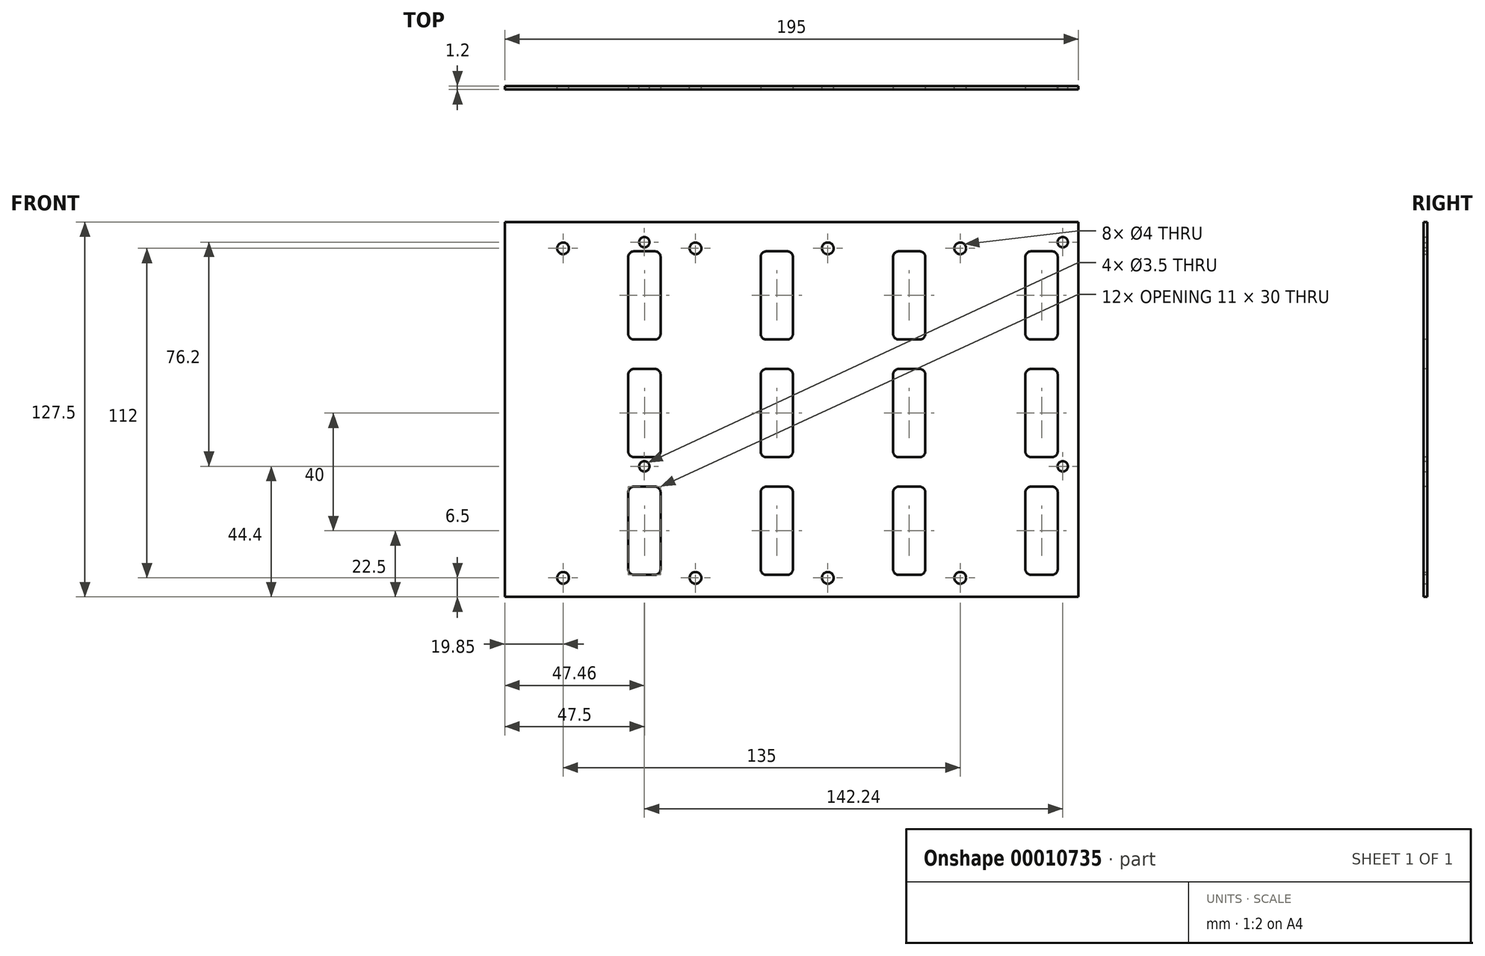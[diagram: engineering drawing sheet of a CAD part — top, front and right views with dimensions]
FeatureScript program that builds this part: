
annotation { "Feature Type Name" : "Feature", "Feature Type Description" : "" }
export const myFeature = defineFeature(function(context is Context, id is Id, definition is map)
    precondition{}
    {
        {
            var Q0;
            Q0=qCreatedBy(makeId("Front.planeOp"),FACE);
            var sketch = newSketch(context, id + "F0", { "sketchPlane" : qUnion([Q0])});
            skLineSegment(sketch, "E0.bottom", {"start": v(0, 0) * mm, "end": v(200, 0) * mm});
            skLineSegment(sketch, "E0.top", {"start": v(0, 130) * mm, "end": v(200, 130) * mm});
            skLineSegment(sketch, "E0.left", {"start": v(0, 0) * mm, "end": v(0, 130) * mm});
            skLineSegment(sketch, "E0.right", {"start": v(200, 0) * mm, "end": v(200, 130) * mm});
            skCircle(sketch, "E1", {"center": v(24.85, 9) * mm, "radius": 2 * mm});
            skCircle(sketch, "E2.0.1.0", {"center": v(24.85, 121) * mm, "radius": 2 * mm});
            skCircle(sketch, "E2.1.0.0", {"center": v(69.85, 9) * mm, "radius": 2 * mm});
            skCircle(sketch, "E2.1.1.0", {"center": v(69.85, 121) * mm, "radius": 2 * mm});
            skCircle(sketch, "E2.2.0.0", {"center": v(114.85, 9) * mm, "radius": 2 * mm});
            skCircle(sketch, "E2.2.1.0", {"center": v(114.85, 121) * mm, "radius": 2 * mm});
            skLineSegment(sketch, "E2.direction1", {"start": v(24.85, 9) * mm, "end": v(69.85, 9) * mm, "construction": true});
            skLineSegment(sketch, "E2.direction2", {"start": v(24.85, 9) * mm, "end": v(24.85, 121) * mm, "construction": true});
            skCircle(sketch, "E3.0.3.0", {"center": v(159.85, 9) * mm, "radius": 2 * mm});
            skCircle(sketch, "E3.0.3.1", {"center": v(159.85, 121) * mm, "radius": 2 * mm});
            skLineSegment(sketch, "E4", {"start": v(200, 65) * mm, "end": v(0, 65) * mm, "construction": true});
            skPoint(sketch, "E4.endSnap0", {"position": v(0, 65) * mm});
            skPoint(sketch, "E4.endSnap1", {"position": v(24.85, 65) * mm});
            skSolve(sketch);
        }
        {
            var Q0;
            Q0=makeQuery(id+"F0.imprint","IMPRINT",FACE,{"disambiguationData":[TD([[makeQuery(id+"F0.imprint","IMPRINT",EDGE,{"derivedFrom":sQuery(id+"F0.wireOp",EDGE,"E0.bottom")}),1.0]])]});
            extrude(context, id + "F1", {"entities" : qUnion([Q0]), "depth" : 1.2 * mm});
        }
        {
            var Q0;
            Q0=makeQuery(id+"F1.opExtrude","CAP_FACE",FACE,{"disambiguationData":[OSD([sQuery(id+"F0.wireOp",EDGE,"E0.bottom"),sQuery(id+"F0.wireOp",EDGE,"E0.top"),sQuery(id+"F0.wireOp",EDGE,"E0.left"),sQuery(id+"F0.wireOp",EDGE,"E0.right"),sQuery(id+"F0.wireOp",EDGE,"E1"),sQuery(id+"F0.wireOp",EDGE,"E2.0.1.0"),sQuery(id+"F0.wireOp",EDGE,"E2.1.0.0"),sQuery(id+"F0.wireOp",EDGE,"E2.1.1.0"),sQuery(id+"F0.wireOp",EDGE,"E2.2.0.0"),sQuery(id+"F0.wireOp",EDGE,"E2.2.1.0"),sQuery(id+"F0.wireOp",EDGE,"E3.0.3.0"),sQuery(id+"F0.wireOp",EDGE,"E3.0.3.1")])],"isStart":false});
            var sketch = newSketch(context, id + "F2", { "sketchPlane" : qUnion([Q0])});
            skLineSegment(sketch, "E5.bottom", {"start": v(49, 10) * mm, "end": v(56, 10) * mm});
            skLineSegment(sketch, "E5.top", {"start": v(49, 40) * mm, "end": v(56, 40) * mm});
            skLineSegment(sketch, "E5.left", {"start": v(47, 12) * mm, "end": v(47, 38) * mm});
            skLineSegment(sketch, "E5.right", {"start": v(58, 12) * mm, "end": v(58, 38) * mm});
            skPoint(sketch, "E6", {"position": v(24.85, 9) * mm});
            skLineSegment(sketch, "E7.bottom", {"start": v(49, 50) * mm, "end": v(56, 50) * mm});
            skLineSegment(sketch, "E7.top", {"start": v(49, 80) * mm, "end": v(56, 80) * mm});
            skLineSegment(sketch, "E7.left", {"start": v(47, 52) * mm, "end": v(47, 78) * mm});
            skLineSegment(sketch, "E7.right", {"start": v(58, 52) * mm, "end": v(58, 78) * mm});
            skLineSegment(sketch, "E8.bottom", {"start": v(49, 90) * mm, "end": v(56, 90) * mm});
            skLineSegment(sketch, "E8.top", {"start": v(49, 120) * mm, "end": v(56, 120) * mm});
            skLineSegment(sketch, "E8.left", {"start": v(47, 92) * mm, "end": v(47, 118) * mm});
            skLineSegment(sketch, "E8.right", {"start": v(58, 92) * mm, "end": v(58, 118) * mm});
            skLineSegment(sketch, "E9", {"start": v(0, 65) * mm, "end": v(200, 65) * mm, "construction": true});
            skPoint(sketch, "E10.visualSharp", {"position": v(47, 40) * mm});
            skArc(sketch, "E10.filletArc", {"start": v(49, 40) * mm, "mid": v(47.59, 39.41) * mm, "end": v(47, 38) * mm});
            skPoint(sketch, "E11.visualSharp", {"position": v(58, 40) * mm});
            skArc(sketch, "E11.filletArc", {"start": v(58, 38) * mm, "mid": v(57.41, 39.41) * mm, "end": v(56, 40) * mm});
            skPoint(sketch, "E12.visualSharp", {"position": v(58, 10) * mm});
            skArc(sketch, "E12.filletArc", {"start": v(56, 10) * mm, "mid": v(57.41, 10.59) * mm, "end": v(58, 12) * mm});
            skPoint(sketch, "E13.visualSharp", {"position": v(47, 10) * mm});
            skArc(sketch, "E13.filletArc", {"start": v(47, 12) * mm, "mid": v(47.59, 10.59) * mm, "end": v(49, 10) * mm});
            skPoint(sketch, "E14.visualSharp", {"position": v(47, 50) * mm});
            skArc(sketch, "E14.filletArc", {"start": v(47, 52) * mm, "mid": v(47.59, 50.59) * mm, "end": v(49, 50) * mm});
            skPoint(sketch, "E15.visualSharp", {"position": v(58, 50) * mm});
            skArc(sketch, "E15.filletArc", {"start": v(56, 50) * mm, "mid": v(57.41, 50.59) * mm, "end": v(58, 52) * mm});
            skPoint(sketch, "E16.visualSharp", {"position": v(47, 80) * mm});
            skArc(sketch, "E16.filletArc", {"start": v(49, 80) * mm, "mid": v(47.59, 79.41) * mm, "end": v(47, 78) * mm});
            skPoint(sketch, "E17.visualSharp", {"position": v(58, 80) * mm});
            skArc(sketch, "E17.filletArc", {"start": v(58, 78) * mm, "mid": v(57.41, 79.41) * mm, "end": v(56, 80) * mm});
            skPoint(sketch, "E18.visualSharp", {"position": v(58, 90) * mm});
            skArc(sketch, "E18.filletArc", {"start": v(56, 90) * mm, "mid": v(57.41, 90.59) * mm, "end": v(58, 92) * mm});
            skPoint(sketch, "E19.visualSharp", {"position": v(47, 90) * mm});
            skArc(sketch, "E19.filletArc", {"start": v(47, 92) * mm, "mid": v(47.59, 90.59) * mm, "end": v(49, 90) * mm});
            skPoint(sketch, "E20.visualSharp", {"position": v(47, 120) * mm});
            skArc(sketch, "E20.filletArc", {"start": v(49, 120) * mm, "mid": v(47.59, 119.41) * mm, "end": v(47, 118) * mm});
            skPoint(sketch, "E21.visualSharp", {"position": v(58, 120) * mm});
            skArc(sketch, "E21.filletArc", {"start": v(58, 118) * mm, "mid": v(57.41, 119.41) * mm, "end": v(56, 120) * mm});
            skPoint(sketch, "E22.1.0.0", {"position": v(103, 120) * mm});
            skPoint(sketch, "E22.1.0.1", {"position": v(103, 90) * mm});
            skPoint(sketch, "E22.1.0.2", {"position": v(92, 80) * mm});
            skPoint(sketch, "E22.1.0.3", {"position": v(92, 10) * mm});
            skPoint(sketch, "E22.1.0.4", {"position": v(103, 80) * mm});
            skPoint(sketch, "E22.1.0.5", {"position": v(103, 40) * mm});
            skPoint(sketch, "E22.1.0.6", {"position": v(92, 40) * mm});
            skPoint(sketch, "E22.1.0.7", {"position": v(92, 90) * mm});
            skLineSegment(sketch, "E22.1.0.8", {"start": v(92, 92) * mm, "end": v(92, 118) * mm});
            skLineSegment(sketch, "E22.1.0.9", {"start": v(103, 92) * mm, "end": v(103, 118) * mm});
            skPoint(sketch, "E22.1.0.10", {"position": v(92, 120) * mm});
            skPoint(sketch, "E22.1.0.11", {"position": v(92, 50) * mm});
            skPoint(sketch, "E22.1.0.12", {"position": v(103, 10) * mm});
            skPoint(sketch, "E22.1.0.13", {"position": v(103, 50) * mm});
            skLineSegment(sketch, "E22.1.0.14", {"start": v(92, 12) * mm, "end": v(92, 38) * mm});
            skLineSegment(sketch, "E22.1.0.15", {"start": v(103, 12) * mm, "end": v(103, 38) * mm});
            skLineSegment(sketch, "E22.1.0.16", {"start": v(92, 52) * mm, "end": v(92, 78) * mm});
            skLineSegment(sketch, "E22.1.0.17", {"start": v(103, 52) * mm, "end": v(103, 78) * mm});
            skArc(sketch, "E22.1.0.18", {"start": v(92, 52) * mm, "mid": v(92.59, 50.59) * mm, "end": v(94, 50) * mm});
            skArc(sketch, "E22.1.0.19", {"start": v(101, 50) * mm, "mid": v(102.41, 50.59) * mm, "end": v(103, 52) * mm});
            skArc(sketch, "E22.1.0.20", {"start": v(92, 92) * mm, "mid": v(92.59, 90.59) * mm, "end": v(94, 90) * mm});
            skArc(sketch, "E22.1.0.21", {"start": v(101, 90) * mm, "mid": v(102.41, 90.59) * mm, "end": v(103, 92) * mm});
            skArc(sketch, "E22.1.0.22", {"start": v(103, 118) * mm, "mid": v(102.41, 119.41) * mm, "end": v(101, 120) * mm});
            skArc(sketch, "E22.1.0.23", {"start": v(94, 80) * mm, "mid": v(92.59, 79.41) * mm, "end": v(92, 78) * mm});
            skArc(sketch, "E22.1.0.24", {"start": v(94, 120) * mm, "mid": v(92.59, 119.41) * mm, "end": v(92, 118) * mm});
            skArc(sketch, "E22.1.0.25", {"start": v(103, 78) * mm, "mid": v(102.41, 79.41) * mm, "end": v(101, 80) * mm});
            skLineSegment(sketch, "E22.1.0.26", {"start": v(94, 10) * mm, "end": v(101, 10) * mm});
            skLineSegment(sketch, "E22.1.0.27", {"start": v(94, 40) * mm, "end": v(101, 40) * mm});
            skArc(sketch, "E22.1.0.28", {"start": v(101, 10) * mm, "mid": v(102.41, 10.59) * mm, "end": v(103, 12) * mm});
            skLineSegment(sketch, "E22.1.0.29", {"start": v(94, 50) * mm, "end": v(101, 50) * mm});
            skLineSegment(sketch, "E22.1.0.30", {"start": v(94, 80) * mm, "end": v(101, 80) * mm});
            skArc(sketch, "E22.1.0.31", {"start": v(103, 38) * mm, "mid": v(102.41, 39.41) * mm, "end": v(101, 40) * mm});
            skArc(sketch, "E22.1.0.32", {"start": v(94, 40) * mm, "mid": v(92.59, 39.41) * mm, "end": v(92, 38) * mm});
            skLineSegment(sketch, "E22.1.0.33", {"start": v(94, 90) * mm, "end": v(101, 90) * mm});
            skLineSegment(sketch, "E22.1.0.34", {"start": v(94, 120) * mm, "end": v(101, 120) * mm});
            skArc(sketch, "E22.1.0.35", {"start": v(92, 12) * mm, "mid": v(92.59, 10.59) * mm, "end": v(94, 10) * mm});
            skPoint(sketch, "E22.2.0.0", {"position": v(148, 120) * mm});
            skPoint(sketch, "E22.2.0.1", {"position": v(148, 90) * mm});
            skPoint(sketch, "E22.2.0.2", {"position": v(137, 80) * mm});
            skPoint(sketch, "E22.2.0.3", {"position": v(137, 10) * mm});
            skPoint(sketch, "E22.2.0.4", {"position": v(148, 80) * mm});
            skPoint(sketch, "E22.2.0.5", {"position": v(148, 40) * mm});
            skPoint(sketch, "E22.2.0.6", {"position": v(137, 40) * mm});
            skPoint(sketch, "E22.2.0.7", {"position": v(137, 90) * mm});
            skLineSegment(sketch, "E22.2.0.8", {"start": v(137, 92) * mm, "end": v(137, 118) * mm});
            skLineSegment(sketch, "E22.2.0.9", {"start": v(148, 92) * mm, "end": v(148, 118) * mm});
            skPoint(sketch, "E22.2.0.10", {"position": v(137, 120) * mm});
            skPoint(sketch, "E22.2.0.11", {"position": v(137, 50) * mm});
            skPoint(sketch, "E22.2.0.12", {"position": v(148, 10) * mm});
            skPoint(sketch, "E22.2.0.13", {"position": v(148, 50) * mm});
            skLineSegment(sketch, "E22.2.0.14", {"start": v(137, 12) * mm, "end": v(137, 38) * mm});
            skLineSegment(sketch, "E22.2.0.15", {"start": v(148, 12) * mm, "end": v(148, 38) * mm});
            skLineSegment(sketch, "E22.2.0.16", {"start": v(137, 52) * mm, "end": v(137, 78) * mm});
            skLineSegment(sketch, "E22.2.0.17", {"start": v(148, 52) * mm, "end": v(148, 78) * mm});
            skArc(sketch, "E22.2.0.18", {"start": v(137, 52) * mm, "mid": v(137.59, 50.59) * mm, "end": v(139, 50) * mm});
            skArc(sketch, "E22.2.0.19", {"start": v(146, 50) * mm, "mid": v(147.41, 50.59) * mm, "end": v(148, 52) * mm});
            skArc(sketch, "E22.2.0.20", {"start": v(137, 92) * mm, "mid": v(137.59, 90.59) * mm, "end": v(139, 90) * mm});
            skArc(sketch, "E22.2.0.21", {"start": v(146, 90) * mm, "mid": v(147.41, 90.59) * mm, "end": v(148, 92) * mm});
            skArc(sketch, "E22.2.0.22", {"start": v(148, 118) * mm, "mid": v(147.41, 119.41) * mm, "end": v(146, 120) * mm});
            skArc(sketch, "E22.2.0.23", {"start": v(139, 80) * mm, "mid": v(137.59, 79.41) * mm, "end": v(137, 78) * mm});
            skArc(sketch, "E22.2.0.24", {"start": v(139, 120) * mm, "mid": v(137.59, 119.41) * mm, "end": v(137, 118) * mm});
            skArc(sketch, "E22.2.0.25", {"start": v(148, 78) * mm, "mid": v(147.41, 79.41) * mm, "end": v(146, 80) * mm});
            skLineSegment(sketch, "E22.2.0.26", {"start": v(139, 10) * mm, "end": v(146, 10) * mm});
            skLineSegment(sketch, "E22.2.0.27", {"start": v(139, 40) * mm, "end": v(146, 40) * mm});
            skArc(sketch, "E22.2.0.28", {"start": v(146, 10) * mm, "mid": v(147.41, 10.59) * mm, "end": v(148, 12) * mm});
            skLineSegment(sketch, "E22.2.0.29", {"start": v(139, 50) * mm, "end": v(146, 50) * mm});
            skLineSegment(sketch, "E22.2.0.30", {"start": v(139, 80) * mm, "end": v(146, 80) * mm});
            skArc(sketch, "E22.2.0.31", {"start": v(148, 38) * mm, "mid": v(147.41, 39.41) * mm, "end": v(146, 40) * mm});
            skArc(sketch, "E22.2.0.32", {"start": v(139, 40) * mm, "mid": v(137.59, 39.41) * mm, "end": v(137, 38) * mm});
            skLineSegment(sketch, "E22.2.0.33", {"start": v(139, 90) * mm, "end": v(146, 90) * mm});
            skLineSegment(sketch, "E22.2.0.34", {"start": v(139, 120) * mm, "end": v(146, 120) * mm});
            skArc(sketch, "E22.2.0.35", {"start": v(137, 12) * mm, "mid": v(137.59, 10.59) * mm, "end": v(139, 10) * mm});
            skPoint(sketch, "E22.3.0.0", {"position": v(193, 120) * mm});
            skPoint(sketch, "E22.3.0.1", {"position": v(193, 90) * mm});
            skPoint(sketch, "E22.3.0.2", {"position": v(182, 80) * mm});
            skPoint(sketch, "E22.3.0.3", {"position": v(182, 10) * mm});
            skPoint(sketch, "E22.3.0.4", {"position": v(193, 80) * mm});
            skPoint(sketch, "E22.3.0.5", {"position": v(193, 40) * mm});
            skPoint(sketch, "E22.3.0.6", {"position": v(182, 40) * mm});
            skPoint(sketch, "E22.3.0.7", {"position": v(182, 90) * mm});
            skLineSegment(sketch, "E22.3.0.8", {"start": v(182, 92) * mm, "end": v(182, 118) * mm});
            skLineSegment(sketch, "E22.3.0.9", {"start": v(193, 92) * mm, "end": v(193, 118) * mm});
            skPoint(sketch, "E22.3.0.10", {"position": v(182, 120) * mm});
            skPoint(sketch, "E22.3.0.11", {"position": v(182, 50) * mm});
            skPoint(sketch, "E22.3.0.12", {"position": v(193, 10) * mm});
            skPoint(sketch, "E22.3.0.13", {"position": v(193, 50) * mm});
            skLineSegment(sketch, "E22.3.0.14", {"start": v(182, 12) * mm, "end": v(182, 38) * mm});
            skLineSegment(sketch, "E22.3.0.15", {"start": v(193, 12) * mm, "end": v(193, 38) * mm});
            skLineSegment(sketch, "E22.3.0.16", {"start": v(182, 52) * mm, "end": v(182, 78) * mm});
            skLineSegment(sketch, "E22.3.0.17", {"start": v(193, 52) * mm, "end": v(193, 78) * mm});
            skArc(sketch, "E22.3.0.18", {"start": v(182, 52) * mm, "mid": v(182.59, 50.59) * mm, "end": v(184, 50) * mm});
            skArc(sketch, "E22.3.0.19", {"start": v(191, 50) * mm, "mid": v(192.41, 50.59) * mm, "end": v(193, 52) * mm});
            skArc(sketch, "E22.3.0.20", {"start": v(182, 92) * mm, "mid": v(182.59, 90.59) * mm, "end": v(184, 90) * mm});
            skArc(sketch, "E22.3.0.21", {"start": v(191, 90) * mm, "mid": v(192.41, 90.59) * mm, "end": v(193, 92) * mm});
            skArc(sketch, "E22.3.0.22", {"start": v(193, 118) * mm, "mid": v(192.41, 119.41) * mm, "end": v(191, 120) * mm});
            skArc(sketch, "E22.3.0.23", {"start": v(184, 80) * mm, "mid": v(182.59, 79.41) * mm, "end": v(182, 78) * mm});
            skArc(sketch, "E22.3.0.24", {"start": v(184, 120) * mm, "mid": v(182.59, 119.41) * mm, "end": v(182, 118) * mm});
            skArc(sketch, "E22.3.0.25", {"start": v(193, 78) * mm, "mid": v(192.41, 79.41) * mm, "end": v(191, 80) * mm});
            skLineSegment(sketch, "E22.3.0.26", {"start": v(184, 10) * mm, "end": v(191, 10) * mm});
            skLineSegment(sketch, "E22.3.0.27", {"start": v(184, 40) * mm, "end": v(191, 40) * mm});
            skArc(sketch, "E22.3.0.28", {"start": v(191, 10) * mm, "mid": v(192.41, 10.59) * mm, "end": v(193, 12) * mm});
            skLineSegment(sketch, "E22.3.0.29", {"start": v(184, 50) * mm, "end": v(191, 50) * mm});
            skLineSegment(sketch, "E22.3.0.30", {"start": v(184, 80) * mm, "end": v(191, 80) * mm});
            skArc(sketch, "E22.3.0.31", {"start": v(193, 38) * mm, "mid": v(192.41, 39.41) * mm, "end": v(191, 40) * mm});
            skArc(sketch, "E22.3.0.32", {"start": v(184, 40) * mm, "mid": v(182.59, 39.41) * mm, "end": v(182, 38) * mm});
            skLineSegment(sketch, "E22.3.0.33", {"start": v(184, 90) * mm, "end": v(191, 90) * mm});
            skLineSegment(sketch, "E22.3.0.34", {"start": v(184, 120) * mm, "end": v(191, 120) * mm});
            skArc(sketch, "E22.3.0.35", {"start": v(182, 12) * mm, "mid": v(182.59, 10.59) * mm, "end": v(184, 10) * mm});
            skLineSegment(sketch, "E22.direction1", {"start": v(58, 120) * mm, "end": v(103, 120) * mm, "construction": true});
            skSolve(sketch);
        }
        {
            var Q0;
            Q0 = qSketchRegion(id + "F2", true);
            extrude(context, id + "F3", {"entities" : qUnion([Q0]), "operationType" : NewBodyOperationType.REMOVE, "oppositeDirection" : true, "depth" : 25 * mm});
        }
        {
            var Q0;
            Q0=makeQuery(id+"F1.opExtrude","CAP_FACE",FACE,{"disambiguationData":[OSD([sQuery(id+"F0.wireOp",EDGE,"E0.bottom"),sQuery(id+"F0.wireOp",EDGE,"E0.top"),sQuery(id+"F0.wireOp",EDGE,"E0.left"),sQuery(id+"F0.wireOp",EDGE,"E0.right"),sQuery(id+"F0.wireOp",EDGE,"E1"),sQuery(id+"F0.wireOp",EDGE,"E2.0.1.0"),sQuery(id+"F0.wireOp",EDGE,"E2.1.0.0"),sQuery(id+"F0.wireOp",EDGE,"E2.1.1.0"),sQuery(id+"F0.wireOp",EDGE,"E2.2.0.0"),sQuery(id+"F0.wireOp",EDGE,"E2.2.1.0"),sQuery(id+"F0.wireOp",EDGE,"E3.0.3.0"),sQuery(id+"F0.wireOp",EDGE,"E3.0.3.1")])],"isStart":true});
            var sketch = newSketch(context, id + "F4", { "sketchPlane" : qUnion([Q0])});
            skCircle(sketch, "E23", {"center": v(-194.7, 123.1) * mm, "radius": 1.75 * mm});
            skCircle(sketch, "E24", {"center": v(-194.7, 46.9) * mm, "radius": 1.75 * mm});
            skCircle(sketch, "E25", {"center": v(-52.46, 46.9) * mm, "radius": 1.75 * mm});
            skCircle(sketch, "E26", {"center": v(-52.46, 123.1) * mm, "radius": 1.75 * mm});
            skSolve(sketch);
        }
        {
            var Q0;
            Q0 = qSketchRegion(id + "F4", true);
            extrude(context, id + "F5", {"entities" : qUnion([Q0]), "operationType" : NewBodyOperationType.REMOVE, "oppositeDirection" : true, "depth" : 25 * mm});
        }
        {
            var Q0;
            Q0=makeQuery(id+"F1.opExtrude","CAP_FACE",FACE,{"disambiguationData":[OSD([sQuery(id+"F0.wireOp",EDGE,"E0.bottom"),sQuery(id+"F0.wireOp",EDGE,"E0.top"),sQuery(id+"F0.wireOp",EDGE,"E0.left"),sQuery(id+"F0.wireOp",EDGE,"E0.right"),sQuery(id+"F0.wireOp",EDGE,"E1"),sQuery(id+"F0.wireOp",EDGE,"E2.0.1.0"),sQuery(id+"F0.wireOp",EDGE,"E2.1.0.0"),sQuery(id+"F0.wireOp",EDGE,"E2.1.1.0"),sQuery(id+"F0.wireOp",EDGE,"E2.2.0.0"),sQuery(id+"F0.wireOp",EDGE,"E2.2.1.0"),sQuery(id+"F0.wireOp",EDGE,"E3.0.3.0"),sQuery(id+"F0.wireOp",EDGE,"E3.0.3.1")])],"isStart":true});
            var sketch = newSketch(context, id + "F6", { "sketchPlane" : qUnion([Q0])});
            skLineSegment(sketch, "E27.bottom", {"start": v(-200, 130) * mm, "end": v(-5, 130) * mm});
            skLineSegment(sketch, "E27.top", {"start": v(-200, 2.5) * mm, "end": v(-5, 2.5) * mm});
            skLineSegment(sketch, "E27.left", {"start": v(-200, 130) * mm, "end": v(-200, 2.5) * mm});
            skLineSegment(sketch, "E27.right", {"start": v(-5, 130) * mm, "end": v(-5, 2.5) * mm});
            skSolve(sketch);
        }
        {
            var Q0;
            {var subQ0=sQuery(id+"F6.wireOp",EDGE,"E27.top");Q0=makeQuery(id+"F6.imprint","IMPRINT",FACE,{"disambiguationData":[TD([[makeQuery(id+"F6.imprint","IMPRINT",EDGE,{"derivedFrom":subQ0}),-1.0]])]});}
            extrude(context, id + "F7", {"entities" : qUnion([Q0]), "operationType" : NewBodyOperationType.REMOVE, "oppositeDirection" : true, "depth" : 25 * mm});
        }
    });
